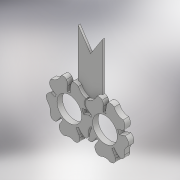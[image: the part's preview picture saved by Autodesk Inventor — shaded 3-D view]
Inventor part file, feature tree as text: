
AUTODESK INVENTOR PART (.ipt)
format: ipt  version: 2017 (Build 210142000, 142)  size: 261,120 bytes
history: native  units: mm
features: extrude x2, sketch x2
ambient origin geometry x8: Origin, YZ Plane, XZ Plane, XY Plane, X Axis, Y Axis, Z Axis, Center Point
bodies: Solid1 (feature_tree)
feature tree (4):
  extrude  "Extrusion1"  Depth=4.0mm
  extrude  "Extrusion2"  Depth=1.5mm
  sketch  "Sketch1"  dims[d0=18.0mm d1=18.0mm d2=21.0mm d3=21.0mm d4=4.0mm d5=0.0mm d6=35.0mm]
  sketch  "Sketch3"  dims[d7=35.0mm d8=35.0mm d9=1.5mm d10=0.0mm]
